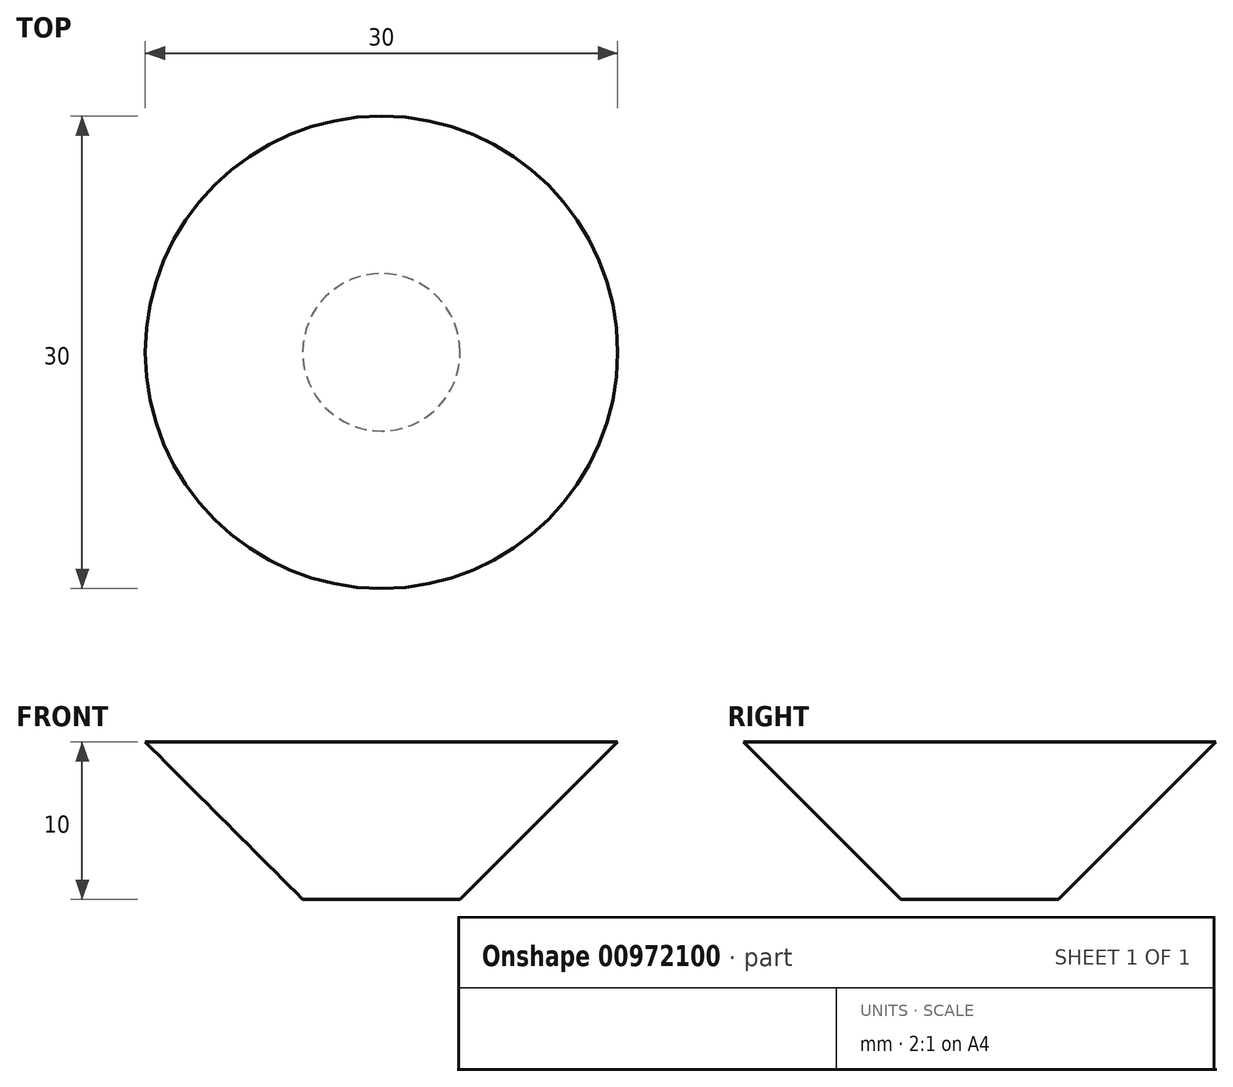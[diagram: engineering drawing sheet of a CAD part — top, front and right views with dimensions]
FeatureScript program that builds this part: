
annotation { "Feature Type Name" : "Feature", "Feature Type Description" : "" }
export const myFeature = defineFeature(function(context is Context, id is Id, definition is map)
    precondition{}
    {
        {
            var Q0;
            Q0=qCreatedBy(makeId("Front.planeOp"),FACE);
            var sketch = newSketch(context, id + "F0", { "sketchPlane" : qUnion([Q0])});
            skLineSegment(sketch, "E0", {"start": v(0, 0) * mm, "end": v(0, 10) * mm});
            skLineSegment(sketch, "E1", {"start": v(0, 10) * mm, "end": v(15, 10) * mm});
            skLineSegment(sketch, "E2", {"start": v(15, 10) * mm, "end": v(5, 0) * mm});
            skLineSegment(sketch, "E3", {"start": v(5, 0) * mm, "end": v(0, 0) * mm});
            skSolve(sketch);
        }
        {
            var Q0;
            Q0=makeQuery(id+"F0.imprint","IMPRINT",FACE,{"disambiguationData":[TD([[makeQuery(id+"F0.imprint","IMPRINT",EDGE,{"derivedFrom":sQuery(id+"F0.wireOp",EDGE,"E0")}),-1.0]])]});
            var Q1;
            Q1=sQuery(id+"F0.wireOp",EDGE,"E0");
            revolve(context, id + "F1", {"surfaceOperationType" : NewSurfaceOperationType.NEW, "entities" : qUnion([Q0]), "axis" : qUnion([Q1]), "revolveType" : RevolveType.FULL});
        }
    });
